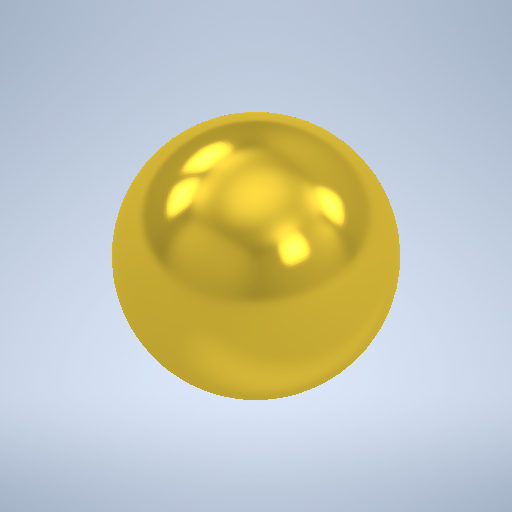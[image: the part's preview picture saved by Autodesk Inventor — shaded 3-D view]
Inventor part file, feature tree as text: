
AUTODESK INVENTOR PART (.ipt)
format: ipt  version: 2025.2 (Build 292293000, 293)  size: 268,288 bytes
history: native  units: mm
features: other x2, sketch x1
ambient origin geometry x8: Origin, YZ Plane, XZ Plane, XY Plane, X Axis, Y Axis, Z Axis, Center Point
bodies: Body1 (feature_tree)
feature tree (3):
  other  "Sólido1"
  other  "Revolução1"
  sketch  "Esboço1"  dims[d1=20.0mm d2=360.0deg d3=0.872665mm]
